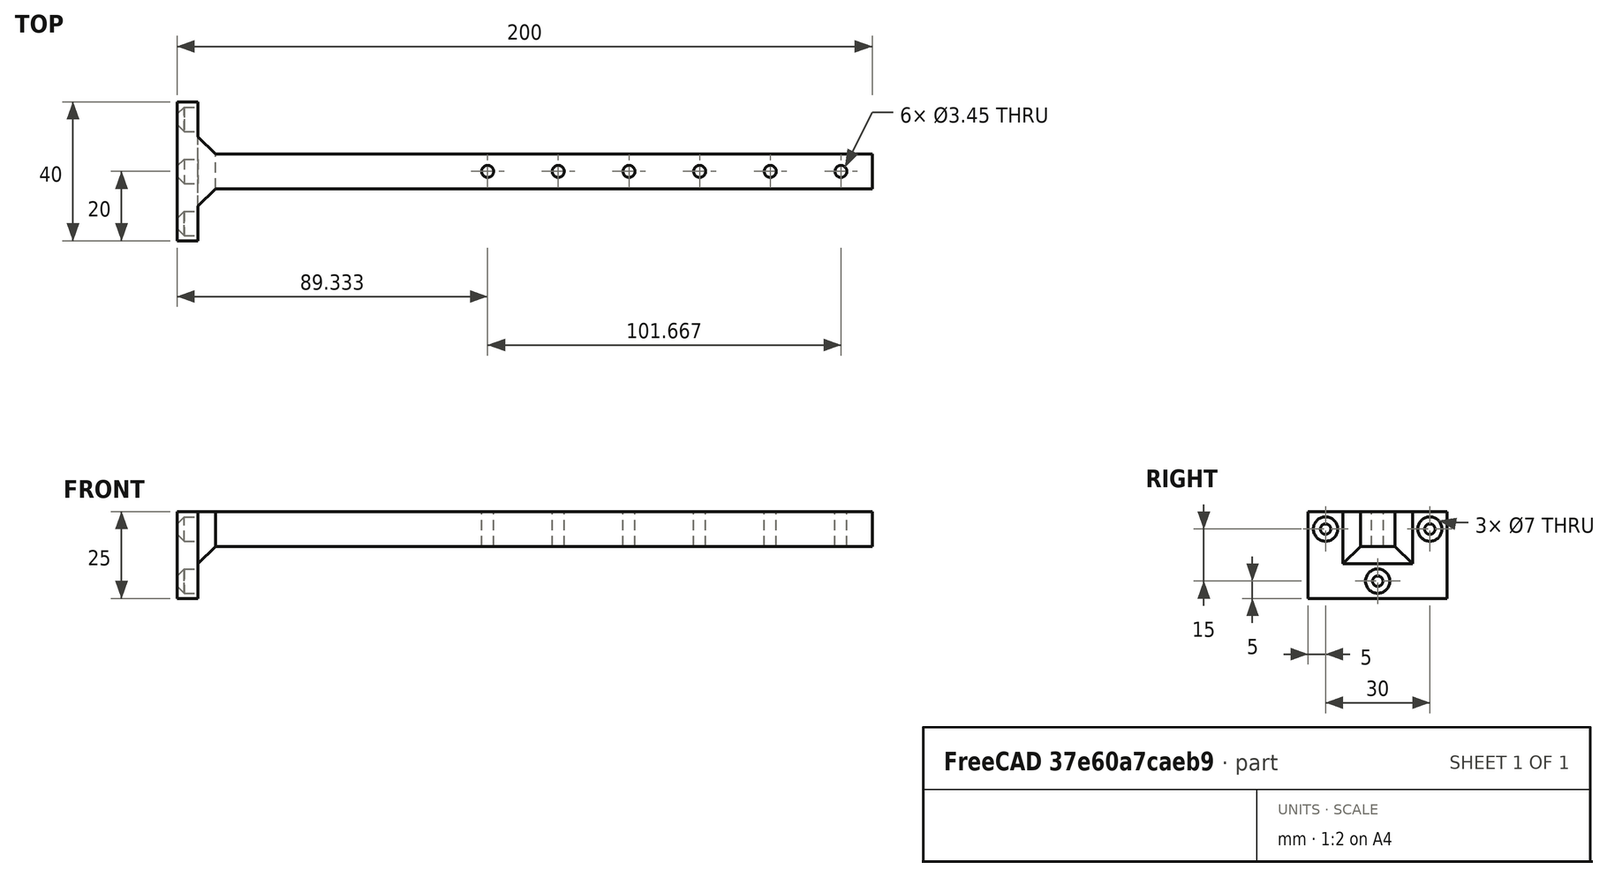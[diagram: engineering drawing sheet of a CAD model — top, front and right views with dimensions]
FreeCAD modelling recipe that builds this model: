
FCSTD DOCUMENT  (FreeCAD 0.16R6703 (Git))
Label: Soporte Tarjetas PCI
License: All rights reserved
LicenseURL: http://en.wikipedia.org/wiki/All_rights_reserved
objects: Part::Cylinder×3, Part::Box×2, Part::FeaturePython×2, Part::Cut×2, Part::MultiFuse×2, Part::Cone×1, Part::Chamfer×1
note: 13 computed .brp shape members not serialized (recipe doc carries the construction recipe); baked Part::Feature solids carry a one-line shape summary decoded from their .brp

FEATURE [Part::Box] Box  label="Cube"
  Height = 10
  Length = 194
  Width = 10
FEATURE [Part::Cylinder] Cylinder
  Angle = 360
  Height = 10
  Placement = pos=(185,5,0) rot=(0,0,1;0rad)
  Radius = 1.725
FEATURE [Part::FeaturePython] Array  # Draft array (typed FeaturePython)
  Angle = 360
  ArrayType = 0
  Axis = (0,0,1)
  Base = -> Cylinder
  Center = (0,0,0)
  Fuse = false
  IntervalAxis = (0,0,0)
  IntervalX = (-20.3333,0,0)
  IntervalY = (0,1,0)
  IntervalZ = (0,0,0)
  NumberPolar = 1
  NumberX = 6
  NumberY = 1
  NumberZ = 1
  expr: IntervalX.x = -122 / 6
FEATURE [Part::Cut] Cut
  Base = -> Box
  Placement = pos=(0,-5,-5) rot=(0,0,1;0rad)
  Tool = -> Array
FEATURE [Part::Cylinder] Cylinder001
  Angle = 360
  Height = 10
  Placement = pos=(15,-5,0) rot=(0,0,1;0rad)
  Radius = 1.5
FEATURE [Part::Cylinder] Cylinder002
  Angle = 360
  Height = 10
  Placement = pos=(15,-5,8) rot=(0,0,1;0rad)
  Radius = 3.5
FEATURE [Part::Cone] Cone
  Angle = 360
  Height = 2
  Placement = pos=(15,-5,6) rot=(0,0,1;0rad)
  Radius1 = 1.5
  Radius2 = 3.5
FEATURE [Part::MultiFuse] Fusion001
  Placement = pos=(0,-10,15) rot=(0,1,0;1.5708rad)
  Shapes = -> [Cylinder001,Cylinder002,Cone]
FEATURE [Part::FeaturePython] Array001  # Draft array (typed FeaturePython)
  Angle = 360
  ArrayType = 1
  Axis = (1,0,0)
  Base = -> Fusion001
  Center = (0,0,0)
  Fuse = false
  IntervalAxis = (0,0,0)
  IntervalX = (1,0,0)
  IntervalY = (0,1,0)
  IntervalZ = (0,0,0)
  NumberPolar = 4
  NumberX = 2
  NumberY = 2
  NumberZ = 1
  Placement = pos=(-6,0,0) rot=(0,0,1;0rad)
FEATURE [Part::Box] Box002  label="Cube002"
  Height = 25
  Length = 6
  Placement = pos=(0,-20,-20) rot=(0,0,1;0rad)
  Width = 40
FEATURE [Part::Cut] Cut001
  Base = -> Box002
  Placement = pos=(-6,0,0) rot=(0,0,1;0rad)
  Tool = -> Array001
FEATURE [Part::MultiFuse] Fusion
  Shapes = -> [Cut,Cut001]
FEATURE [Part::Chamfer] Chamfer
  Base = -> Fusion
  Edges = 3 edges r=5: [Edge6,Edge9,Edge11]
